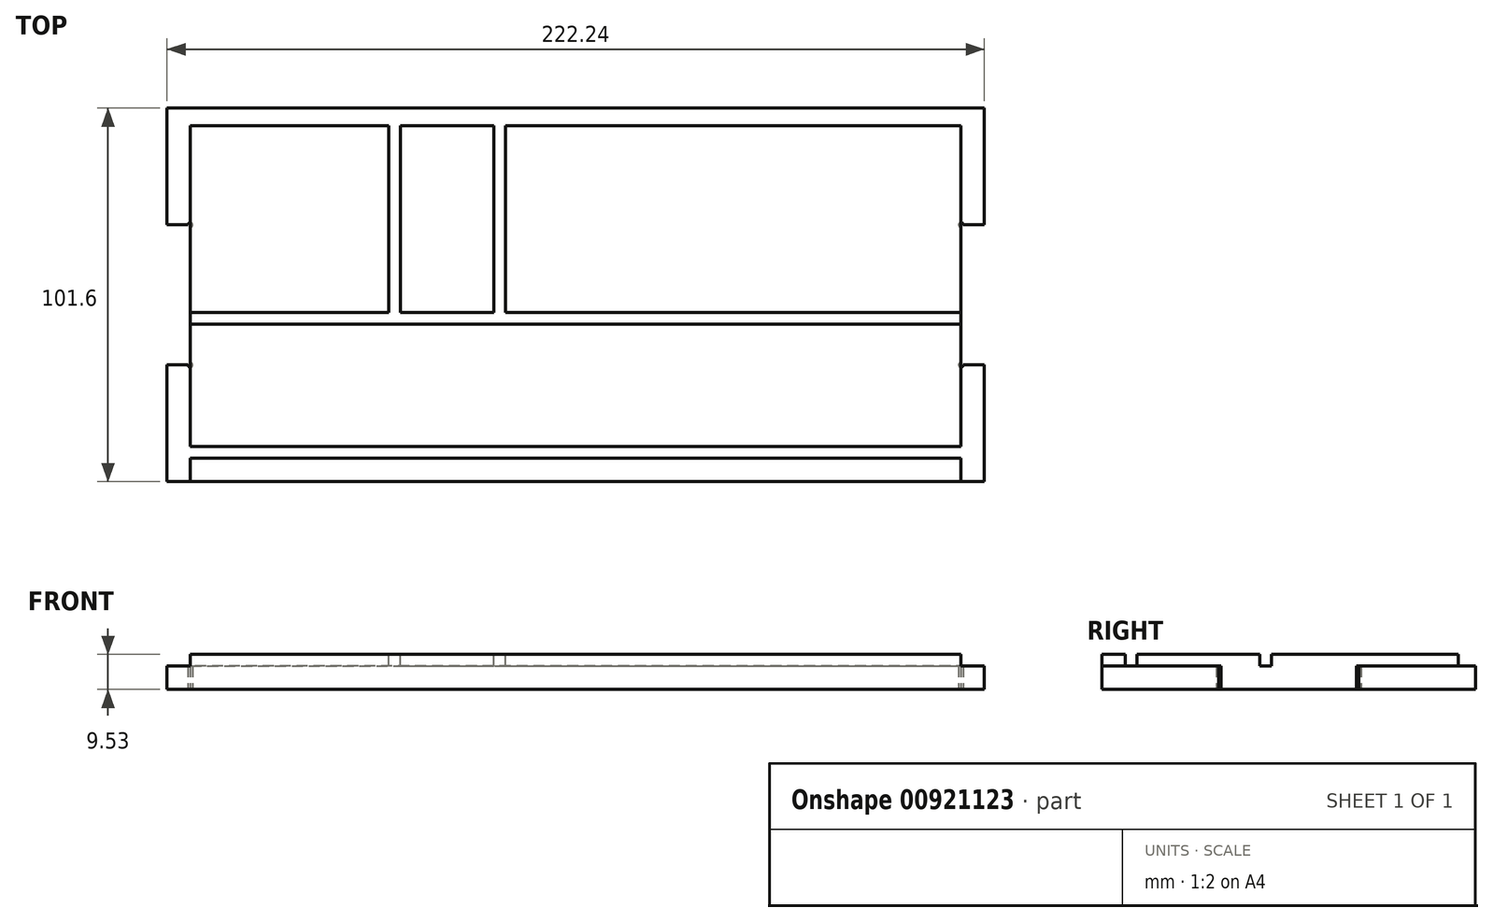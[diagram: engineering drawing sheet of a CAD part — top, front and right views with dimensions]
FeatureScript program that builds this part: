
annotation { "Feature Type Name" : "Feature", "Feature Type Description" : "" }
export const myFeature = defineFeature(function(context is Context, id is Id, definition is map)
    precondition{}
    {
        {
            var Q0;
            Q0=qCreatedBy(makeId("Top.planeOp"),FACE);
            var sketch = newSketch(context, id + "F0", { "sketchPlane" : qUnion([Q0])});
            skLineSegment(sketch, "E0.bottom", {"start": v(111.13, -50.8) * mm, "end": v(-111.12, -50.8) * mm});
            skLineSegment(sketch, "E0.top", {"start": v(111.12, 50.8) * mm, "end": v(-111.13, 50.8) * mm});
            skLineSegment(sketch, "E0.left", {"start": v(111.13, -50.8) * mm, "end": v(111.12, 50.8) * mm});
            skLineSegment(sketch, "E0.right", {"start": v(-111.12, -50.8) * mm, "end": v(-111.13, 50.8) * mm});
            skPoint(sketch, "E0.middle", {"position": v(0, 0) * mm});
            skSolve(sketch);
        }
        {
            var Q0;
            Q0 = qSketchRegion(id + "F0", true);
            extrude(context, id + "F1", {"entities" : qUnion([Q0]), "depth" : 9.52 * mm, "offsetDistance" : 25.4 * mm});
        }
        {
            var Q0;
            Q0=makeQuery(id+"F1.opExtrude","CAP_FACE",FACE,{"disambiguationData":[OSD([sQuery(id+"F0.wireOp",EDGE,"E0.bottom"),sQuery(id+"F0.wireOp",EDGE,"E0.top"),sQuery(id+"F0.wireOp",EDGE,"E0.left"),sQuery(id+"F0.wireOp",EDGE,"E0.right")])],"isStart":false});
            var sketch = newSketch(context, id + "F2", { "sketchPlane" : qUnion([Q0])});
            skLineSegment(sketch, "E1.bottom", {"start": v(-111.13, 19.05) * mm, "end": v(-104.78, 19.05) * mm});
            skLineSegment(sketch, "E1.top", {"start": v(-111.13, -19.05) * mm, "end": v(-104.78, -19.05) * mm});
            skLineSegment(sketch, "E1.left", {"start": v(-111.13, 19.05) * mm, "end": v(-111.13, -19.05) * mm});
            skLineSegment(sketch, "E1.right", {"start": v(-104.78, 19.05) * mm, "end": v(-104.78, -19.05) * mm});
            skLineSegment(sketch, "E2.bottom", {"start": v(111.13, 19.05) * mm, "end": v(104.78, 19.05) * mm});
            skLineSegment(sketch, "E2.top", {"start": v(111.13, -19.05) * mm, "end": v(104.78, -19.05) * mm});
            skLineSegment(sketch, "E2.left", {"start": v(111.13, 19.05) * mm, "end": v(111.13, -19.05) * mm});
            skLineSegment(sketch, "E2.right", {"start": v(104.78, 19.05) * mm, "end": v(104.78, -19.05) * mm});
            skLineSegment(sketch, "E3", {"start": v(-111.13, 0) * mm, "end": v(111.12, 0) * mm, "construction": true});
            skSolve(sketch);
        }
        {
            var Q0;
            Q0 = qSketchRegion(id + "F2", true);
            extrude(context, id + "F3", {"entities" : qUnion([Q0]), "operationType" : NewBodyOperationType.REMOVE, "endBound" : BoundingType.THROUGH_ALL, "oppositeDirection" : true, "depth" : 25.4 * mm, "offsetDistance" : 25.4 * mm});
        }
        {
            var Q0;
            Q0=makeQuery(id+"F1.opExtrude","CAP_FACE",FACE,{"disambiguationData":[OSD([sQuery(id+"F0.wireOp",EDGE,"E0.bottom"),sQuery(id+"F0.wireOp",EDGE,"E0.top"),sQuery(id+"F0.wireOp",EDGE,"E0.left"),sQuery(id+"F0.wireOp",EDGE,"E0.right")])],"isStart":false});
            var sketch = newSketch(context, id + "F4", { "sketchPlane" : qUnion([Q0])});
            skLineSegment(sketch, "E4", {"start": v(-104.78, 19.05) * mm, "end": v(-104.78, 46.02) * mm});
            skLineSegment(sketch, "E5", {"start": v(-104.78, 46.02) * mm, "end": v(104.78, 46.02) * mm});
            skLineSegment(sketch, "E6", {"start": v(104.78, 46.02) * mm, "end": v(104.78, 19.05) * mm});
            skLineSegment(sketch, "E7", {"start": v(104.78, 19.05) * mm, "end": v(111.13, 19.05) * mm});
            skLineSegment(sketch, "E8", {"start": v(111.12, 19.05) * mm, "end": v(111.12, 50.8) * mm});
            skLineSegment(sketch, "E9", {"start": v(111.12, 50.8) * mm, "end": v(-111.13, 50.8) * mm});
            skLineSegment(sketch, "E10", {"start": v(-111.13, 50.8) * mm, "end": v(-111.13, 19.05) * mm});
            skLineSegment(sketch, "E11", {"start": v(-111.13, 19.05) * mm, "end": v(-104.78, 19.05) * mm});
            skLineSegment(sketch, "E12", {"start": v(-104.78, -19.05) * mm, "end": v(-111.13, -19.05) * mm});
            skLineSegment(sketch, "E13", {"start": v(-111.12, -19.05) * mm, "end": v(-111.12, -50.8) * mm});
            skLineSegment(sketch, "E14", {"start": v(111.13, -50.8) * mm, "end": v(111.13, -19.05) * mm});
            skLineSegment(sketch, "E15", {"start": v(111.13, -19.05) * mm, "end": v(104.78, -19.05) * mm});
            skLineSegment(sketch, "E16", {"start": v(104.78, -19.05) * mm, "end": v(104.78, -50.8) * mm});
            skLineSegment(sketch, "E17", {"start": v(-104.78, -50.8) * mm, "end": v(-104.78, -19.05) * mm});
            skLineSegment(sketch, "E18", {"start": v(-104.78, -50.8) * mm, "end": v(-111.12, -50.8) * mm});
            skLineSegment(sketch, "E19", {"start": v(104.78, -50.8) * mm, "end": v(111.13, -50.8) * mm});
            skSolve(sketch);
        }
        {
            var Q0;
            Q0 = qSketchRegion(id + "F4", true);
            extrude(context, id + "F5", {"entities" : qUnion([Q0]), "operationType" : NewBodyOperationType.REMOVE, "oppositeDirection" : true, "depth" : 3.17 * mm, "offsetDistance" : 25.4 * mm});
        }
        {
            var Q0;
            Q0=makeQuery(id+"F1.opExtrude","CAP_FACE",FACE,{"disambiguationData":[OSD([sQuery(id+"F0.wireOp",EDGE,"E0.bottom"),sQuery(id+"F0.wireOp",EDGE,"E0.top"),sQuery(id+"F0.wireOp",EDGE,"E0.left"),sQuery(id+"F0.wireOp",EDGE,"E0.right")])],"isStart":false});
            var sketch = newSketch(context, id + "F6", { "sketchPlane" : qUnion([Q0])});
            skLineSegment(sketch, "E20.bottom", {"start": v(-104.78, -41.28) * mm, "end": v(104.78, -41.27) * mm});
            skLineSegment(sketch, "E20.top", {"start": v(-104.78, -44.45) * mm, "end": v(104.78, -44.45) * mm});
            skLineSegment(sketch, "E20.left", {"start": v(-104.78, -41.27) * mm, "end": v(-104.78, -44.45) * mm});
            skLineSegment(sketch, "E20.right", {"start": v(104.78, -41.27) * mm, "end": v(104.78, -44.45) * mm});
            skLineSegment(sketch, "E21.bottom", {"start": v(-104.78, -4.78) * mm, "end": v(104.78, -4.78) * mm});
            skLineSegment(sketch, "E21.top", {"start": v(-104.78, -7.95) * mm, "end": v(104.78, -7.95) * mm});
            skLineSegment(sketch, "E21.left", {"start": v(-104.78, -4.78) * mm, "end": v(-104.78, -7.95) * mm});
            skLineSegment(sketch, "E21.right", {"start": v(104.78, -4.78) * mm, "end": v(104.78, -7.95) * mm});
            skLineSegment(sketch, "E22", {"start": v(-50.8, 46.02) * mm, "end": v(-47.62, 46.02) * mm});
            skLineSegment(sketch, "E23", {"start": v(-47.62, 46.02) * mm, "end": v(-47.62, -4.78) * mm});
            skLineSegment(sketch, "E24", {"start": v(-50.8, 46.02) * mm, "end": v(-50.8, -4.78) * mm});
            skLineSegment(sketch, "E25", {"start": v(-22.22, -4.78) * mm, "end": v(-22.22, 46.02) * mm});
            skLineSegment(sketch, "E26", {"start": v(-22.22, 46.02) * mm, "end": v(-19.05, 46.02) * mm});
            skLineSegment(sketch, "E27", {"start": v(-19.05, 46.02) * mm, "end": v(-19.05, -4.78) * mm});
            skSolve(sketch);
        }
        {
            var Q0;
            Q0 = qSketchRegion(id + "F6", true);
            extrude(context, id + "F7", {"entities" : qUnion([Q0]), "operationType" : NewBodyOperationType.REMOVE, "oppositeDirection" : true, "depth" : 3.17 * mm, "offsetDistance" : 25.4 * mm});
        }
        {
            var Q0;
            Q0=makeQuery(id+"F1.opExtrude","CAP_FACE",FACE,{"disambiguationData":[OSD([sQuery(id+"F0.wireOp",EDGE,"E0.bottom"),sQuery(id+"F0.wireOp",EDGE,"E0.top"),sQuery(id+"F0.wireOp",EDGE,"E0.left"),sQuery(id+"F0.wireOp",EDGE,"E0.right")])],"isStart":true});
            var sketch = newSketch(context, id + "F8", { "sketchPlane" : qUnion([Q0])});
            skArc(sketch, "E28", {"start": v(104.78, -18.41) * mm, "mid": v(104.33, -19.5) * mm, "end": v(105.4, -19.05) * mm});
            skArc(sketch, "E29", {"start": v(104.78, 18.42) * mm, "mid": v(104.33, 19.5) * mm, "end": v(105.4, 19.05) * mm});
            skArc(sketch, "E30", {"start": v(-104.78, 18.41) * mm, "mid": v(-104.33, 19.5) * mm, "end": v(-105.4, 19.05) * mm});
            skArc(sketch, "E31", {"start": v(-104.78, -18.41) * mm, "mid": v(-104.33, -19.5) * mm, "end": v(-105.4, -19.05) * mm});
            skLineSegment(sketch, "E32", {"start": v(-105.4, 19.05) * mm, "end": v(-104.78, 19.05) * mm});
            skLineSegment(sketch, "E33", {"start": v(-104.78, 19.05) * mm, "end": v(-104.78, 18.41) * mm});
            skLineSegment(sketch, "E34", {"start": v(-104.78, -19.05) * mm, "end": v(-105.4, -19.05) * mm});
            skLineSegment(sketch, "E35", {"start": v(-104.78, -19.05) * mm, "end": v(-104.78, -18.41) * mm});
            skLineSegment(sketch, "E36", {"start": v(104.78, -19.05) * mm, "end": v(105.4, -19.05) * mm});
            skLineSegment(sketch, "E37", {"start": v(104.78, -19.05) * mm, "end": v(104.78, -18.41) * mm});
            skLineSegment(sketch, "E38", {"start": v(104.78, 19.05) * mm, "end": v(104.78, 18.42) * mm});
            skLineSegment(sketch, "E39", {"start": v(104.78, 19.05) * mm, "end": v(105.4, 19.05) * mm});
            skSolve(sketch);
        }
        {
            var Q0;
            Q0 = qSketchRegion(id + "F8", true);
            var Q1;
            Q1=makeQuery(id+"F7.boolean.opBoolean","MERGE",FACE,{"derivedFrom":[makeQuery(id+"F5.boolean.opBoolean","COPY",FACE,{"derivedFrom":makeQuery(id+"F5.opExtrude","CAP_FACE",FACE,{"disambiguationData":[OSD([sQuery(id+"F4.wireOp",EDGE,"E12"),sQuery(id+"F4.wireOp",EDGE,"E13"),sQuery(id+"F4.wireOp",EDGE,"E17"),sQuery(id+"F4.wireOp",EDGE,"E18")])],"isStart":false})}),makeQuery(id+"F5.boolean.opBoolean","COPY",FACE,{"derivedFrom":makeQuery(id+"F5.opExtrude","CAP_FACE",FACE,{"disambiguationData":[OSD([sQuery(id+"F4.wireOp",EDGE,"E14"),sQuery(id+"F4.wireOp",EDGE,"E15"),sQuery(id+"F4.wireOp",EDGE,"E16"),sQuery(id+"F4.wireOp",EDGE,"E19")])],"isStart":false})})],"fromTools":[makeQuery(id+"F7.opExtrude","CAP_FACE",FACE,{"disambiguationData":[OSD([sQuery(id+"F6.wireOp",EDGE,"E20.bottom"),sQuery(id+"F6.wireOp",EDGE,"E20.top"),sQuery(id+"F6.wireOp",EDGE,"E20.left"),sQuery(id+"F6.wireOp",EDGE,"E20.right")])],"isStart":false})]});
            extrude(context, id + "F9", {"entities" : qUnion([Q0]), "operationType" : NewBodyOperationType.REMOVE, "endBound" : BoundingType.UP_TO_SURFACE, "oppositeDirection" : true, "depth" : 25.4 * mm, "endBoundEntityFace" : qUnion([Q1]), "offsetDistance" : 25.4 * mm});
        }
    });
